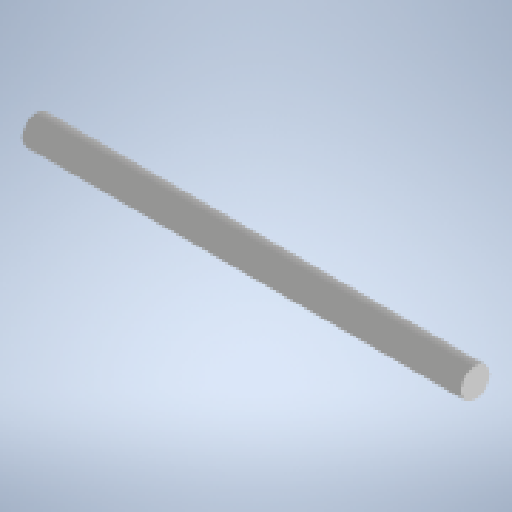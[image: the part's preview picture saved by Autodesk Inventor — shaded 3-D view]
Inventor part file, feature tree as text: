
AUTODESK INVENTOR PART (.ipt)
format: ipt  version: 2025 (Build 290162010, 162A)  size: 146,944 bytes
history: native  units: mm
features: extrude x1, sketch x1
ambient origin geometry x8: Origin, YZ Plane, XZ Plane, XY Plane, X Axis, Y Axis, Z Axis, Center Point
bodies: Volumenkörper1 (feature_tree)
feature tree (2):
  extrude  "Extrusion1"  Depth=30.0mm TaperAngle=0.0deg
  sketch  "Skizze1"  dims[d0=2.0mm d1=30.0mm d2=0.0mm]
